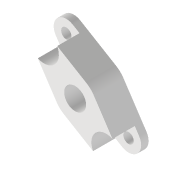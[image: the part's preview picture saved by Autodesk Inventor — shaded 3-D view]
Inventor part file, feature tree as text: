
AUTODESK INVENTOR PART (.ipt)
format: ipt  version: 2022 (Build 260153000, 153)  size: 159,744 bytes
history: native  units: mm
features: reference x6, sketch x4, extrude x3, other x2, hole x1, projected_geometry x1
ambient origin geometry x8: Origin, YZ Plane, XZ Plane, XY Plane, X Axis, Y Axis, Z Axis, Center Point
bodies: Volumenkörper1 (feature_tree)
feature tree (17):
  extrude  "Extrusion1"  Depth=2.0mm
  extrude  "Extrusion2"  Depth=5.9mm
  extrude  "Extrusion3"  [1 undecoded]
  hole  "Bohrung1"  [1 undecoded]
  sketch  "Skizze1"  dims[d0=8.0mm d1=0.0mm d2=2.0mm]
  reference  "Referenz1"
  reference  "Referenz2"
  reference  "Referenz3"
  sketch  "Skizze2"  dims[d3=3.0mm d4=0.0mm d5=5.9mm]
  projected_geometry  "Projizierte Kontur1"
  sketch  "Skizze3"  dims[d6=3.0mm d7=0.0mm]
  reference  "Referenz4"
  reference  "Referenz5"
  reference  "Referenz6"
  sketch  "Skizze4"  dims[d8=2.8mm d9=6.0mm d10=8.0mm d11=6.0mm d12=90.0deg d13=8.0mm d14=20.594885mm]
  other  "Assembly_Matchboxscope_injectionmolded.iam"
  other  "IM_Matchboxscope_base:1"
note: 2 required parameter values undecoded (feature->parameter linkage not recoverable at this tier; creation-order binding heuristic only, values carry confidence <= 0.55)
